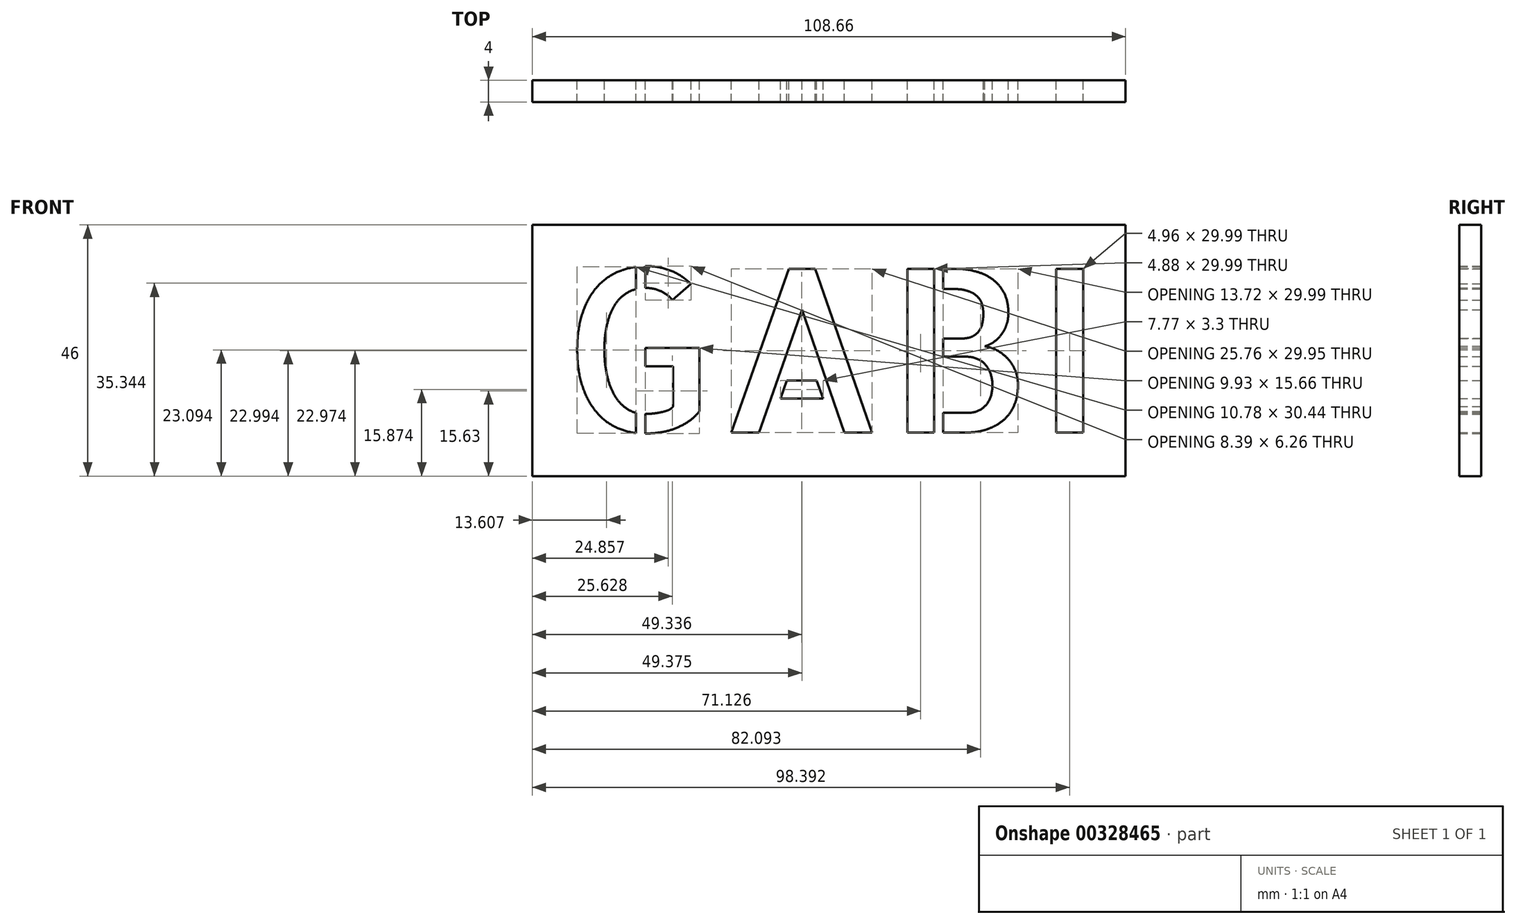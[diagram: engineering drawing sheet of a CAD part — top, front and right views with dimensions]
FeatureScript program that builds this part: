
annotation { "Feature Type Name" : "Feature", "Feature Type Description" : "" }
export const myFeature = defineFeature(function(context is Context, id is Id, definition is map)
    precondition{}
    {
        {
            var Q0;
            Q0=qCreatedBy(makeId("Front.planeOp"),FACE);
            var sketch = newSketch(context, id + "F0", { "sketchPlane" : qUnion([Q0])});
            skText(sketch, "E0", { "text": "GABI", "fontName": "AllertaStencil-Regular.ttf"});
            skLineSegment(sketch, "E1.bottom", {"start": v(7.58, 65.62) * mm, "end": v(116.24, 65.62) * mm});
            skLineSegment(sketch, "E1.top", {"start": v(7.58, 19.62) * mm, "end": v(116.24, 19.62) * mm});
            skLineSegment(sketch, "E1.left", {"start": v(7.58, 65.62) * mm, "end": v(7.58, 19.62) * mm});
            skLineSegment(sketch, "E1.right", {"start": v(116.24, 65.62) * mm, "end": v(116.24, 19.62) * mm});
            skPoint(sketch, "E2", {"position": v(111.24, 42.62) * mm});
            skPoint(sketch, "E3", {"position": v(116.24, 42.62) * mm});
            skPoint(sketch, "E4", {"position": v(61.91, 65.62) * mm});
            const initialGuessF0  = {"E0": [0.01258, 0.02762, 1, 0, 0.03]};
            skSetInitialGuess(sketch, initialGuessF0);
            skSolve(sketch);
        }
        {
            var Q0;
            Q0=makeQuery(id+"F0.imprint","IMPRINT",FACE,{"disambiguationData":[TD([[makeQuery(id+"F0.imprint","IMPRINT",EDGE,{"derivedFrom":sQuery(id+"F0.wireOp",EDGE,"E0.sketch_text.stroke-0")}),1.0]])]});
            extrude(context, id + "F1", {"entities" : qUnion([Q0]), "depth" : 4 * mm});
        }
    });
